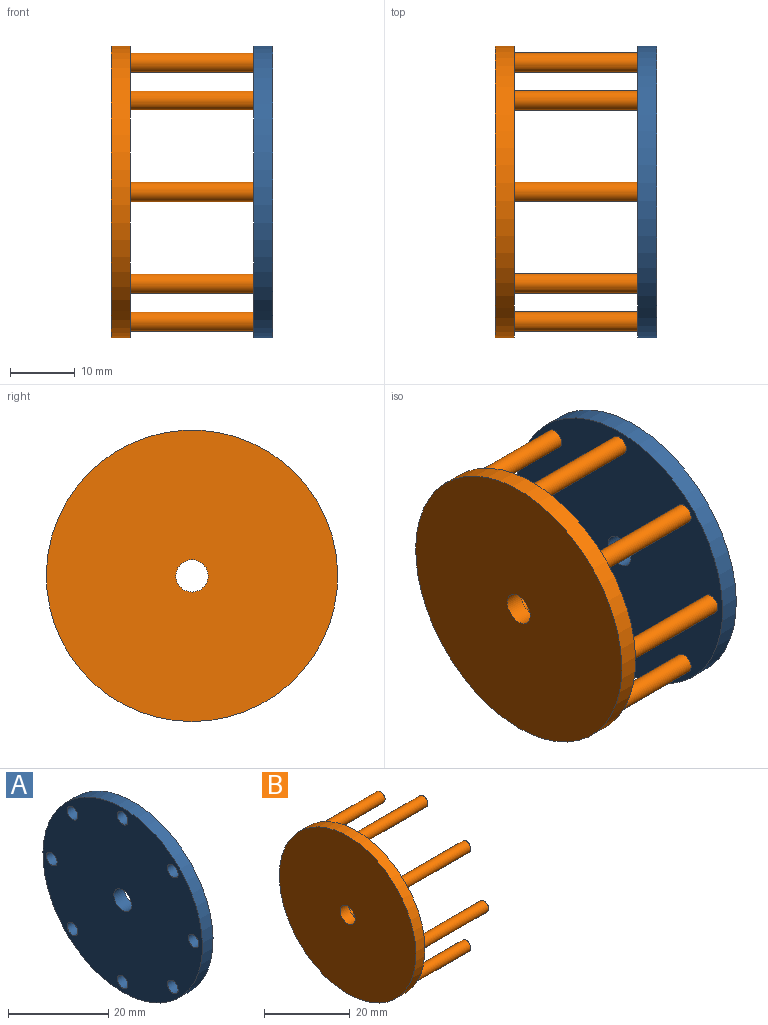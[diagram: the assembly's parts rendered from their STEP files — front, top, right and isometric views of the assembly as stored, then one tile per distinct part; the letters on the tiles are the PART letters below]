
ASSEMBLY  parts=2 mates=1
PART A: 12 faces, bbox 3x45x45 mm
  f0: cylinder r=1.5mm len=3mm, axis (-1,0,0), area 28.3mm2, adj f10,f11
  f1: cylinder r=1.5mm len=3mm, axis (-1,0,0), area 28.3mm2, adj f10,f11
  f2: cylinder r=1.5mm len=3mm, axis (-1,0,0), area 28.3mm2, adj f10,f11
  f3: cylinder r=1.5mm len=3mm, axis (-1,0,0), area 28.3mm2, adj f10,f11
  f4: cylinder r=1.5mm len=3mm, axis (-1,0,0), area 28.3mm2, adj f10,f11
  f5: cylinder r=1.5mm len=3mm, axis (-1,0,0), area 28.3mm2, adj f10,f11
  f6: cylinder r=1.5mm len=3mm, axis (-1,0,0), area 28.3mm2, adj f10,f11
  f7: cylinder r=1.5mm len=3mm, axis (-1,0,0), area 28.3mm2, adj f10,f11
  f8: cylinder r=2.5mm len=5mm, axis (-1,0,0), area 47.1mm2, adj f10,f11
  f9: cylinder r=22.5mm len=45mm, axis (-1,0,0), area 424.1mm2, adj f10,f11
  f10: plane 45x45mm, normal (1,0,0), area 1514.2mm2, adj f0,f1,f2,f3,f4,f5,f6,f7
  f11: plane 45x45mm, normal (-1,0,0), area 1514.2mm2, adj f0,f1,f2,f3,f4,f5,f6,f7
PART B: 20 faces, bbox 25x45x45 mm
  f0: cylinder r=2.5mm len=5mm, axis (-1,0,0), area 47.1mm2, adj f2,f3
  f1: cylinder r=22.5mm len=45mm, axis (-1,0,0), area 424.1mm2, adj f2,f3
  f2: plane 45x45mm, normal (1,0,0), area 1514.2mm2, adj f0,f1,f4,f6,f8,f10,f12,f14
  f3: plane 45x45mm, normal (-1,0,0), area 1570.8mm2, adj f0,f1
  f4: cylinder r=1.5mm len=22mm, axis (-1,0,0), area 207.3mm2, adj f2,f5
  f5: plane 3x3mm, normal (1,0,0), area 7.1mm2, adj f4
  f6: cylinder r=1.5mm len=22mm, axis (-1,0,0), area 207.3mm2, adj f2,f7
  f7: plane 3x3mm, normal (1,0,0), area 7.1mm2, adj f6
  f8: cylinder r=1.5mm len=22mm, axis (-1,0,0), area 207.3mm2, adj f2,f9
  f9: plane 3x3mm, normal (1,0,0), area 7.1mm2, adj f8
  f10: cylinder r=1.5mm len=22mm, axis (-1,0,0), area 207.3mm2, adj f2,f11
  f11: plane 3x3mm, normal (1,0,0), area 7.1mm2, adj f10
  f12: cylinder r=1.5mm len=22mm, axis (-1,0,0), area 207.3mm2, adj f2,f13
  f13: plane 3x3mm, normal (1,0,0), area 7.1mm2, adj f12
  f14: cylinder r=1.5mm len=22mm, axis (-1,0,0), area 207.3mm2, adj f2,f15
  f15: plane 3x3mm, normal (1,0,0), area 7.1mm2, adj f14
  f16: cylinder r=1.5mm len=22mm, axis (-1,0,0), area 207.3mm2, adj f2,f17
  f17: plane 3x3mm, normal (1,0,0), area 7.1mm2, adj f16
  f18: cylinder r=1.5mm len=22mm, axis (-1,0,0), area 207.3mm2, adj f2,f19
  f19: plane 3x3mm, normal (1,0,0), area 7.1mm2, adj f18
PLACE A t=(35.89,3.85,8.82)mm fixed
PLACE B t=(13.89,3.85,8.82)mm fixed
MATE cylindrical B.f6 <-> A.f1  axis (-1,0,0) through (27.89,-10.29,22.97)mm
